# Revit family: APL Residential Thermal Heart Sliding Window FSSF
name_source: partatom
category: Windows
revit_build: Autodesk Revit LT 2017 (Build: 20160225_1515(x64)
units: mm (PartAtom-declared; Revit-internal decimal feet)

## family parameters
Always vertical = Yes
Cut with Voids When Loaded = No
Host = Wall
OmniClass Number = 23.30.20.00
OmniClass Title = Windows
Room Calculation Point = No
Shared = No

## types (2) — shared parameters
Analytic Construction = <None>
Arrow Opening = Yes
Default Sill Height = 900 mm  [stored 2.95276 ft]
Frame Projection Ext. = 14 mm  [stored 0.0459318 ft]
Frame Projection Int. = 20 mm  [stored 0.0656168 ft]
Frame Width = 12 mm  [stored 0.0393701 ft]
Groove = 10 mm  [stored 0.0328084 ft]
Height = 1200 mm
Jamb Liner 1 = Yes
Jamb Liner 2 = Yes
Liner End = 10 mm  [stored 0.0328084 ft]
Liner Head = Yes
Liner Sill = Yes
Rough Height = 1215 mm  [stored 3.98622 ft]
Rough Width = 3215 mm  [stored 10.5479 ft]
Wall Closure = By host
Width = 3200 mm  [stored 10.4987 ft]

## per-type parameters (varying)
| type | Reveal Liner |
| Liner | Yes |
| Architrave | No |

type visibility flags (boolean, named after types; folded from table):
- Liner: Yes: (none)
- Architrave: Yes: Architrave

note: [stored X ft] marks values corroborated as IEEE doubles in the binary element streams (Revit-internal decimal feet)

## geometry (parser evidence)
native form markers: Sweep x24
no freeform markers — native parametric forms only
